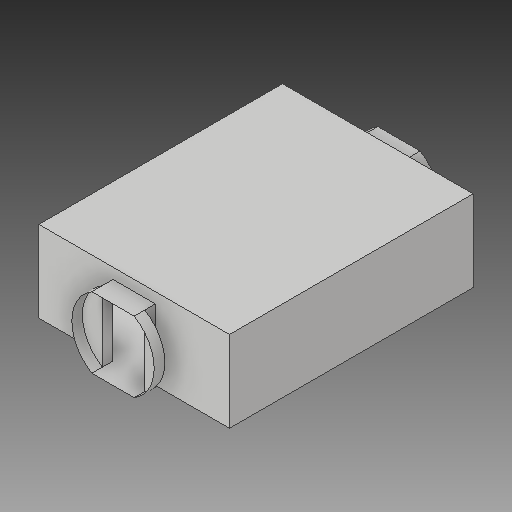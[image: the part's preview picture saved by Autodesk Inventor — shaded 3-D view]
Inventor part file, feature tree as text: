
AUTODESK INVENTOR PART (.ipt)
format: ipt  version: 2017 (Build 210142000, 142)  size: 183,296 bytes
history: native  units: in
note: dims shown in document units (in); Inventor stores cm internally (conversion verified against a paired STEP export)
features: extrude x5, sketch x5, other x1, mirror x1, delete_face x1
ambient origin geometry x8: Origin, YZ Plane, XZ Plane, XY Plane, X Axis, Y Axis, Z Axis, Center Point
bodies: Solid1 (feature_tree)
feature tree (13):
  extrude  "floor"  Depth=25.0in
  extrude  "walls"  Depth=1.0in
  extrude  "doorframe"  Depth=1.0in
  extrude  "ceiling"  Depth=1.0in TaperAngle=0.0deg
  sketch  "Sketch10"  dims[d17=2.0in d18=6.6667in d20=8.6667in d21=0.0in d22=1.0in d23=0.0in d37=6.6667in d40=1.0in d41=0.0in d58=4.0in d60=3.8873in d61=3.8873in d65=1.6458in d71=3.3333in d73=1.0in d76=1.0in]
  extrude  "corridor connect"  Depth=6.6667in
  other  "middle of the room"
  mirror  "Mirror connection for starting door"
  delete_face  "Delete Face1"
  sketch  "Sketch1"  dims[d0=20.0in d1=25.0in]
  sketch  "Sketch4"  dims[d2=1.0in d3=0.0in d11=1.0in]
  sketch  "Sketch5"  dims[d12=1.0in d13=1.0in]
  sketch  "Sketch7"  dims[d14=1.0in d15=8.6667in d16=0.0in]
